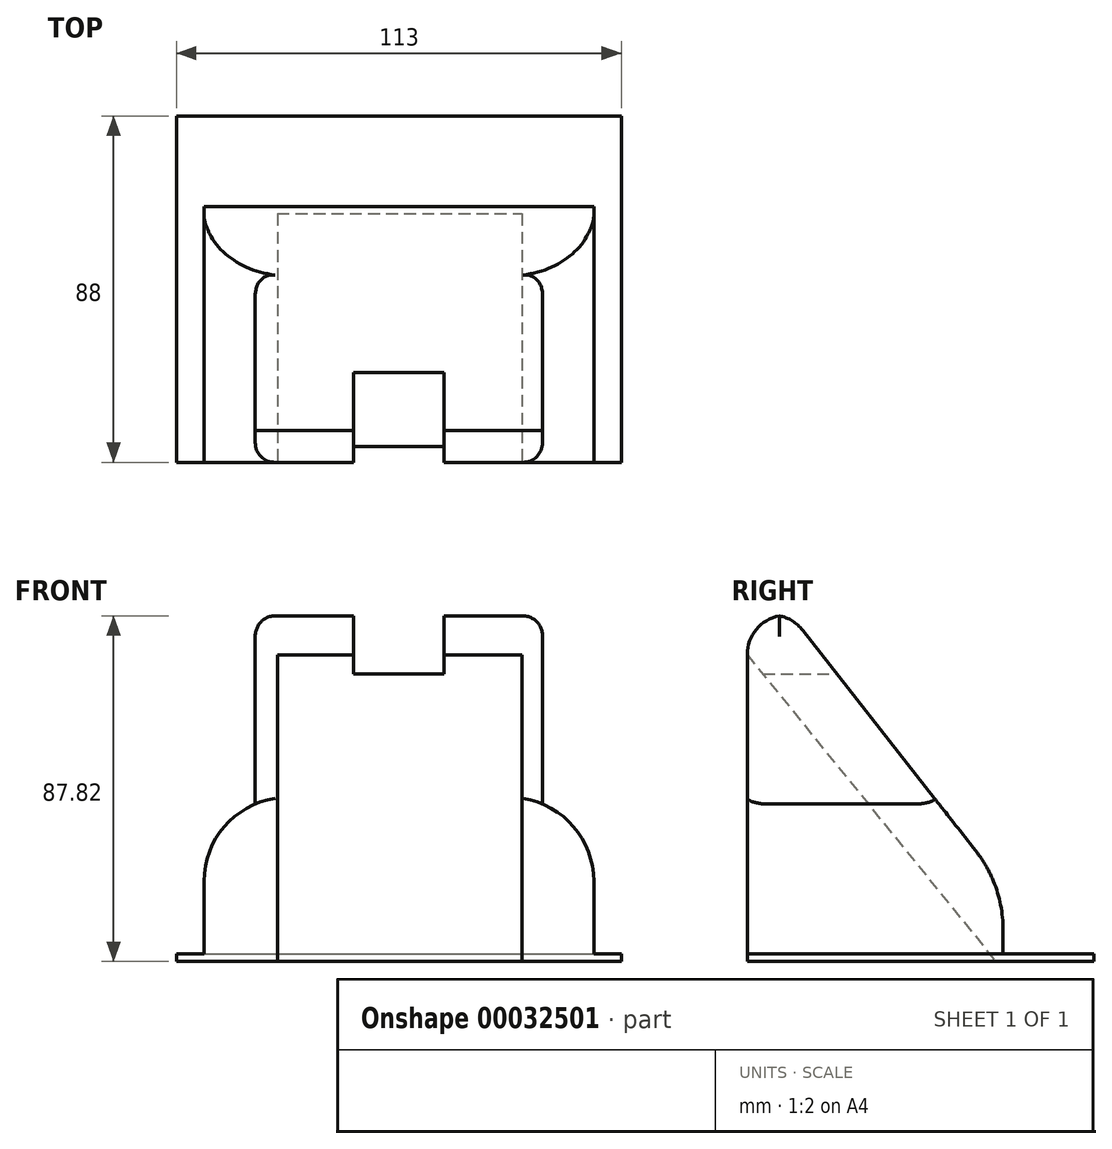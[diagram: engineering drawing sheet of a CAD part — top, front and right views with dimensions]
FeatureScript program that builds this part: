
annotation { "Feature Type Name" : "Feature", "Feature Type Description" : "" }
export const myFeature = defineFeature(function(context is Context, id is Id, definition is map)
    precondition{}
    {
        {
            var Q0;
            Q0=qCreatedBy(makeId("Front.planeOp"),FACE);
            var sketch = newSketch(context, id + "F0", { "sketchPlane" : qUnion([Q0])});
            skLineSegment(sketch, "E0", {"start": v(-13.43, 0) * mm, "end": v(-13.43, 2) * mm});
            skLineSegment(sketch, "E1", {"start": v(-13.43, 2) * mm, "end": v(-6.43, 2) * mm});
            skLineSegment(sketch, "E2", {"start": v(-6.43, 2) * mm, "end": v(-6.43, 40) * mm});
            skLineSegment(sketch, "E3", {"start": v(-6.43, 40) * mm, "end": v(6.57, 40) * mm});
            skLineSegment(sketch, "E4", {"start": v(6.57, 40) * mm, "end": v(6.57, 88) * mm});
            skLineSegment(sketch, "E5", {"start": v(6.57, 88) * mm, "end": v(31.57, 88) * mm});
            skLineSegment(sketch, "E6", {"start": v(31.57, 88) * mm, "end": v(31.57, 73) * mm});
            skLineSegment(sketch, "E7", {"start": v(31.57, 73) * mm, "end": v(43.07, 73) * mm});
            skLineSegment(sketch, "E8", {"start": v(-13.43, 0) * mm, "end": v(10.57, 0) * mm});
            skLineSegment(sketch, "E9.MirrorCS", {"start": v(54.57, 73) * mm, "end": v(43.07, 73) * mm});
            skLineSegment(sketch, "E10.MirrorCS", {"start": v(54.57, 88) * mm, "end": v(54.57, 73) * mm});
            skLineSegment(sketch, "E11.MirrorCS", {"start": v(79.57, 88) * mm, "end": v(54.57, 88) * mm});
            skLineSegment(sketch, "E12.MirrorCS", {"start": v(79.57, 40) * mm, "end": v(79.57, 88) * mm});
            skLineSegment(sketch, "E13.MirrorCS", {"start": v(92.57, 40) * mm, "end": v(79.57, 40) * mm});
            skLineSegment(sketch, "E14.MirrorCS", {"start": v(92.57, 2) * mm, "end": v(92.57, 40) * mm});
            skLineSegment(sketch, "E15.MirrorCS", {"start": v(99.57, 2) * mm, "end": v(92.57, 2) * mm});
            skLineSegment(sketch, "E16.MirrorCS", {"start": v(99.57, 0) * mm, "end": v(99.57, 2) * mm});
            skLineSegment(sketch, "E17.MirrorCS", {"start": v(99.57, 0) * mm, "end": v(75.57, 0) * mm});
            skLineSegment(sketch, "E18", {"start": v(75.57, 0) * mm, "end": v(10.57, 0) * mm});
            skSolve(sketch);
        }
        {
            var Q0;
            Q0 = qSketchRegion(id + "F0", true);
            extrude(context, id + "F1", {"entities" : qUnion([Q0]), "depth" : 88 * mm});
        }
        {
            var Q0;
            Q0=qCreatedBy(makeId("Right.planeOp"),FACE);
            var sketch = newSketch(context, id + "F2", { "sketchPlane" : qUnion([Q0])});
            skLineSegment(sketch, "E19", {"start": v(-77.05, 90.68) * mm, "end": v(-77.05, 88.18) * mm});
            skLineSegment(sketch, "E20", {"start": v(-77.05, 88.18) * mm, "end": v(-22.72, 18.86) * mm});
            skLineSegment(sketch, "E21", {"start": v(-22.72, 18.86) * mm, "end": v(2.44, 18.86) * mm});
            skLineSegment(sketch, "E22", {"start": v(2.44, 18.86) * mm, "end": v(2.44, 90.4) * mm});
            skLineSegment(sketch, "E23", {"start": v(2.44, 90.4) * mm, "end": v(-77.05, 90.68) * mm});
            skSolve(sketch);
        }
        {
            var Q0;
            Q0 = qSketchRegion(id + "F2", true);
            extrude(context, id + "F3", {"entities" : qUnion([Q0]), "operationType" : NewBodyOperationType.REMOVE, "endBound" : BoundingType.SYMMETRIC, "oppositeDirection" : true, "depth" : 424.15 * mm});
        }
        {
            var Q0;
            Q0=makeQuery(id+"F3.boolean.opBoolean","INTERSECT",EDGE,{"derivedFrom":[makeQuery(id+"F1.opExtrude","SWEPT_FACE",FACE,{"disambiguationData":[OSD([sQuery(id+"F0.wireOp",EDGE,"E5")])]}),makeQuery(id+"F3.opExtrude","SWEPT_FACE",FACE,{"disambiguationData":[OSD([sQuery(id+"F2.wireOp",EDGE,"E20")])]})]});
            var Q1;
            Q1=makeQuery(id+"F1.opExtrude","CAP_EDGE",EDGE,{"disambiguationData":[OSD([sQuery(id+"F0.wireOp",EDGE,"E5")])],"isStart":false});
            var Q2;
            Q2=makeQuery(id+"F3.boolean.opBoolean","INTERSECT",EDGE,{"derivedFrom":[makeQuery(id+"F1.opExtrude","SWEPT_FACE",FACE,{"disambiguationData":[OSD([sQuery(id+"F0.wireOp",EDGE,"E11.MirrorCS")])]}),makeQuery(id+"F3.opExtrude","SWEPT_FACE",FACE,{"disambiguationData":[OSD([sQuery(id+"F2.wireOp",EDGE,"E20")])]})]});
            var Q3;
            Q3=makeQuery(id+"F1.opExtrude","CAP_EDGE",EDGE,{"disambiguationData":[OSD([sQuery(id+"F0.wireOp",EDGE,"E11.MirrorCS")])],"isStart":false});
            fillet(context, id + "F4", {"entities" : qUnion([Q0, Q1, Q2, Q3]), "radius" : 10 * mm, "tangentPropagation" : true, "allowEdgeOverflow" : false});
        }
        {
            var Q0;
            Q0=makeQuery(id+"F1.opExtrude","SWEPT_EDGE",EDGE,{"disambiguationData":[OSD([sQuery(id+"F0.wireOp",EDGE,"E2"),sQuery(id+"F0.wireOp",EDGE,"E3")])]});
            var Q1;
            Q1=makeQuery(id+"F1.opExtrude","SWEPT_EDGE",EDGE,{"disambiguationData":[OSD([sQuery(id+"F0.wireOp",EDGE,"E13.MirrorCS"),sQuery(id+"F0.wireOp",EDGE,"E14.MirrorCS")])]});
            fillet(context, id + "F5", {"entities" : qUnion([Q0, Q1]), "radius" : 21.28 * mm, "tangentPropagation" : true, "allowEdgeOverflow" : false});
        }
        {
            var Q0;
            Q0=makeQuery(id+"F4.opFillet","BLEND_EDGE",EDGE,{"blendedFrom":[makeQuery(id+"F1.opExtrude","CAP_EDGE",EDGE,{"disambiguationData":[OSD([sQuery(id+"F0.wireOp",EDGE,"E5")])],"isStart":false}),makeQuery(id+"F1.opExtrude","SWEPT_FACE",FACE,{"disambiguationData":[OSD([sQuery(id+"F0.wireOp",EDGE,"E4")])]})],"blendedInto":[makeQuery(id+"F1.opExtrude","SWEPT_FACE",FACE,{"disambiguationData":[OSD([sQuery(id+"F0.wireOp",EDGE,"E4")])]})]});
            var Q1;
            Q1=makeQuery(id+"F4.opFillet","BLEND_EDGE",EDGE,{"blendedFrom":[makeQuery(id+"F3.boolean.opBoolean","INTERSECT",EDGE,{"derivedFrom":[makeQuery(id+"F1.opExtrude","SWEPT_FACE",FACE,{"disambiguationData":[OSD([sQuery(id+"F0.wireOp",EDGE,"E5")])]}),makeQuery(id+"F3.opExtrude","SWEPT_FACE",FACE,{"disambiguationData":[OSD([sQuery(id+"F2.wireOp",EDGE,"E20")])]})]}),makeQuery(id+"F1.opExtrude","SWEPT_FACE",FACE,{"disambiguationData":[OSD([sQuery(id+"F0.wireOp",EDGE,"E4")])]})],"blendedInto":[makeQuery(id+"F1.opExtrude","SWEPT_FACE",FACE,{"disambiguationData":[OSD([sQuery(id+"F0.wireOp",EDGE,"E4")])]})]});
            fillet(context, id + "F6", {"entities" : qUnion([Q0, Q1]), "radius" : 5 * mm, "tangentPropagation" : true, "allowEdgeOverflow" : false});
        }
        {
            var Q0;
            Q0=makeQuery(id+"F4.opFillet","BLEND_EDGE",EDGE,{"blendedFrom":[makeQuery(id+"F3.boolean.opBoolean","INTERSECT",EDGE,{"derivedFrom":[makeQuery(id+"F1.opExtrude","SWEPT_FACE",FACE,{"disambiguationData":[OSD([sQuery(id+"F0.wireOp",EDGE,"E11.MirrorCS")])]}),makeQuery(id+"F3.opExtrude","SWEPT_FACE",FACE,{"disambiguationData":[OSD([sQuery(id+"F2.wireOp",EDGE,"E20")])]})]}),makeQuery(id+"F1.opExtrude","SWEPT_FACE",FACE,{"disambiguationData":[OSD([sQuery(id+"F0.wireOp",EDGE,"E12.MirrorCS")])]})],"blendedInto":[makeQuery(id+"F1.opExtrude","SWEPT_FACE",FACE,{"disambiguationData":[OSD([sQuery(id+"F0.wireOp",EDGE,"E12.MirrorCS")])]})]});
            var Q1;
            Q1=makeQuery(id+"F4.opFillet","BLEND_EDGE",EDGE,{"blendedFrom":[makeQuery(id+"F1.opExtrude","CAP_EDGE",EDGE,{"disambiguationData":[OSD([sQuery(id+"F0.wireOp",EDGE,"E11.MirrorCS")])],"isStart":false}),makeQuery(id+"F1.opExtrude","SWEPT_FACE",FACE,{"disambiguationData":[OSD([sQuery(id+"F0.wireOp",EDGE,"E12.MirrorCS")])]})],"blendedInto":[makeQuery(id+"F1.opExtrude","SWEPT_FACE",FACE,{"disambiguationData":[OSD([sQuery(id+"F0.wireOp",EDGE,"E12.MirrorCS")])]})]});
            fillet(context, id + "F7", {"entities" : qUnion([Q0, Q1]), "radius" : 5 * mm, "tangentPropagation" : true, "allowEdgeOverflow" : false});
        }
        {
            var Q0;
            Q0=qCreatedBy(makeId("Top.planeOp"),FACE);
            cPlane(context, id + "F8", {"entities" : qUnion([Q0]), "cplaneType" : CPlaneType.OFFSET, "offset" : 2 * mm, "width" : 150 * mm, "height" : 150 * mm});
        }
        {
            var Q0;
            Q0=qCreatedBy(id+"F8.planeOp",FACE);
            var sketch = newSketch(context, id + "F9", { "sketchPlane" : qUnion([Q0])});
            skLineSegment(sketch, "E24.bottom", {"start": v(-9.1, 0) * mm, "end": v(95.42, 0) * mm});
            skLineSegment(sketch, "E24.top", {"start": v(-9.1, -23.02) * mm, "end": v(95.42, -23.02) * mm});
            skLineSegment(sketch, "E24.left", {"start": v(-9.1, 0) * mm, "end": v(-9.1, -23.02) * mm});
            skLineSegment(sketch, "E24.right", {"start": v(95.42, 0) * mm, "end": v(95.42, -23.02) * mm});
            skSolve(sketch);
        }
        {
            var Q0;
            Q0 = qSketchRegion(id + "F9", true);
            extrude(context, id + "F10", {"entities" : qUnion([Q0]), "operationType" : NewBodyOperationType.REMOVE, "depth" : 45.88 * mm});
        }
        {
            var Q0;
            Q0=makeQuery(id+"F10.boolean.opBoolean","INTERSECT",EDGE,{"derivedFrom":[makeQuery(id+"F3.boolean.opBoolean","COPY",FACE,{"derivedFrom":makeQuery(id+"F3.opExtrude","SWEPT_FACE",FACE,{"disambiguationData":[OSD([sQuery(id+"F2.wireOp",EDGE,"E20")])]})}),makeQuery(id+"F10.opExtrude","SWEPT_FACE",FACE,{"disambiguationData":[OSD([sQuery(id+"F9.wireOp",EDGE,"E24.top")])]})]});
            fillet(context, id + "F11", {"entities" : qUnion([Q0]), "radius" : 32.4 * mm, "tangentPropagation" : true, "allowEdgeOverflow" : false});
        }
        {
            var Q0;
            Q0=makeQuery(id+"F1.opExtrude","SWEPT_FACE",FACE,{"disambiguationData":[OSD([sQuery(id+"F0.wireOp",EDGE,"E16.MirrorCS")])]});
            cPlane(context, id + "F12", {"entities" : qUnion([Q0]), "cplaneType" : CPlaneType.OFFSET, "offset" : 25.26 * mm, "oppositeDirection" : true, "width" : 150 * mm, "height" : 150 * mm});
        }
        {
            var Q0;
            Q0=qCreatedBy(id+"F12.planeOp",FACE);
            var sketch = newSketch(context, id + "F13", { "sketchPlane" : qUnion([Q0])});
            skLineSegment(sketch, "E25", {"start": v(-88.03, 0) * mm, "end": v(-88.03, 77.97) * mm});
            skLineSegment(sketch, "E26", {"start": v(-88.03, 77.97) * mm, "end": v(-24.85, 0) * mm});
            skLineSegment(sketch, "E27", {"start": v(-24.85, 0) * mm, "end": v(-88.03, 0) * mm});
            skSolve(sketch);
        }
        {
            var Q0;
            Q0 = qSketchRegion(id + "F13", true);
            extrude(context, id + "F14", {"entities" : qUnion([Q0]), "operationType" : NewBodyOperationType.REMOVE, "oppositeDirection" : true, "depth" : 62.1 * mm});
        }
    });
